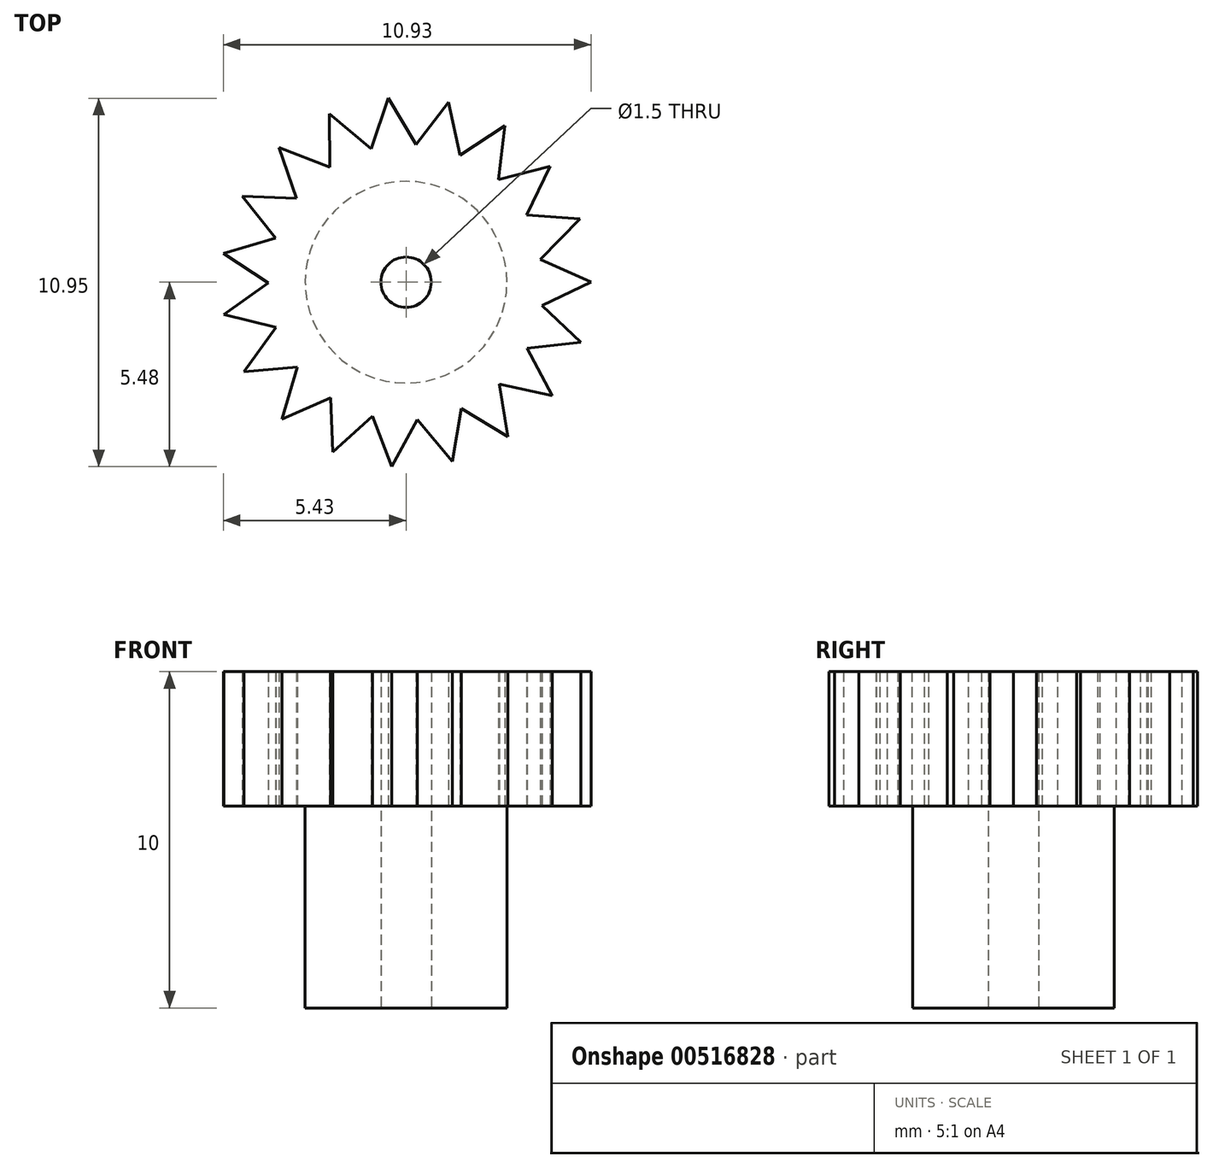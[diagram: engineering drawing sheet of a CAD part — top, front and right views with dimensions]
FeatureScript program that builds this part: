
annotation { "Feature Type Name" : "Feature", "Feature Type Description" : "" }
export const myFeature = defineFeature(function(context is Context, id is Id, definition is map)
    precondition{}
    {
        {
            var Q0;
            Q0=qCreatedBy(makeId("Top.planeOp"),FACE);
            var sketch = newSketch(context, id + "F0", { "sketchPlane" : qUnion([Q0])});
            skCircle(sketch, "E0", {"center": v(0, 0) * mm, "radius": 3 * mm});
            skSolve(sketch);
        }
        {
            var Q0;
            Q0 = qSketchRegion(id + "F0", true);
            extrude(context, id + "F1", {"entities" : qUnion([Q0]), "depth" : 6 * mm, "offsetDistance" : 25.4 * mm});
        }
        {
            var Q0;
            Q0=makeQuery(id+"F1.opExtrude","CAP_FACE",FACE,{"disambiguationData":[OSD([sQuery(id+"F0.wireOp",EDGE,"E0")])],"isStart":false});
            var sketch = newSketch(context, id + "F2", { "sketchPlane" : qUnion([Q0])});
            skLineSegment(sketch, "E1", {"start": v(5.5, 0) * mm, "end": v(3.99, 0.68) * mm});
            skLineSegment(sketch, "E2", {"start": v(5.5, 0) * mm, "end": v(4.04, -0.7) * mm});
            skPoint(sketch, "E3.start.orphan", {"position": v(4, 0) * mm});
            skLineSegment(sketch, "E4.1.0", {"start": v(5.2, -1.78) * mm, "end": v(4.04, -0.7) * mm});
            skLineSegment(sketch, "E4.1.1", {"start": v(5.2, -1.78) * mm, "end": v(3.6, -1.96) * mm});
            skLineSegment(sketch, "E4.2.0", {"start": v(4.35, -3.37) * mm, "end": v(3.6, -1.96) * mm});
            skLineSegment(sketch, "E4.2.1", {"start": v(4.35, -3.37) * mm, "end": v(2.77, -3.02) * mm});
            skLineSegment(sketch, "E4.3.0", {"start": v(3.02, -4.6) * mm, "end": v(2.77, -3.02) * mm});
            skLineSegment(sketch, "E4.3.1", {"start": v(3.02, -4.6) * mm, "end": v(1.64, -3.76) * mm});
            skLineSegment(sketch, "E4.4.0", {"start": v(1.37, -5.33) * mm, "end": v(1.64, -3.76) * mm});
            skLineSegment(sketch, "E4.4.1", {"start": v(1.37, -5.33) * mm, "end": v(0.34, -4.09) * mm});
            skLineSegment(sketch, "E4.5.0", {"start": v(-0.43, -5.48) * mm, "end": v(0.34, -4.09) * mm});
            skLineSegment(sketch, "E4.5.1", {"start": v(-0.43, -5.48) * mm, "end": v(-1, -3.98) * mm});
            skLineSegment(sketch, "E4.6.0", {"start": v(-2.18, -5.05) * mm, "end": v(-1, -3.98) * mm});
            skLineSegment(sketch, "E4.6.1", {"start": v(-2.18, -5.05) * mm, "end": v(-2.24, -3.44) * mm});
            skLineSegment(sketch, "E4.7.0", {"start": v(-3.7, -4.07) * mm, "end": v(-2.24, -3.44) * mm});
            skLineSegment(sketch, "E4.7.1", {"start": v(-3.7, -4.07) * mm, "end": v(-3.23, -2.53) * mm});
            skLineSegment(sketch, "E4.8.0", {"start": v(-4.82, -2.66) * mm, "end": v(-3.23, -2.53) * mm});
            skLineSegment(sketch, "E4.8.1", {"start": v(-4.82, -2.66) * mm, "end": v(-3.87, -1.35) * mm});
            skLineSegment(sketch, "E4.9.0", {"start": v(-5.42, -0.96) * mm, "end": v(-3.87, -1.35) * mm});
            skLineSegment(sketch, "E4.9.1", {"start": v(-5.42, -0.96) * mm, "end": v(-4.1, -0.02) * mm});
            skLineSegment(sketch, "E4.10.0", {"start": v(-5.43, 0.85) * mm, "end": v(-4.1, -0.02) * mm});
            skLineSegment(sketch, "E4.10.1", {"start": v(-5.43, 0.85) * mm, "end": v(-3.89, 1.3) * mm});
            skLineSegment(sketch, "E4.11.0", {"start": v(-4.87, 2.56) * mm, "end": v(-3.89, 1.3) * mm});
            skLineSegment(sketch, "E4.11.1", {"start": v(-4.87, 2.56) * mm, "end": v(-3.25, 2.5) * mm});
            skLineSegment(sketch, "E4.12.0", {"start": v(-3.77, 4) * mm, "end": v(-3.25, 2.5) * mm});
            skLineSegment(sketch, "E4.12.1", {"start": v(-3.77, 4) * mm, "end": v(-2.27, 3.42) * mm});
            skLineSegment(sketch, "E4.13.0", {"start": v(-2.28, 5) * mm, "end": v(-2.27, 3.42) * mm});
            skLineSegment(sketch, "E4.13.1", {"start": v(-2.28, 5) * mm, "end": v(-1.04, 3.97) * mm});
            skLineSegment(sketch, "E4.14.0", {"start": v(-0.53, 5.47) * mm, "end": v(-1.04, 3.97) * mm});
            skLineSegment(sketch, "E4.14.1", {"start": v(-0.53, 5.47) * mm, "end": v(0.3, 4.1) * mm});
            skLineSegment(sketch, "E4.15.0", {"start": v(1.27, 5.35) * mm, "end": v(0.3, 4.1) * mm});
            skLineSegment(sketch, "E4.15.1", {"start": v(1.27, 5.35) * mm, "end": v(1.6, 3.77) * mm});
            skLineSegment(sketch, "E4.16.0", {"start": v(2.93, 4.65) * mm, "end": v(1.6, 3.77) * mm});
            skLineSegment(sketch, "E4.16.1", {"start": v(2.93, 4.65) * mm, "end": v(2.74, 3.05) * mm});
            skLineSegment(sketch, "E4.17.0", {"start": v(4.28, 3.45) * mm, "end": v(2.74, 3.05) * mm});
            skLineSegment(sketch, "E4.17.1", {"start": v(4.28, 3.45) * mm, "end": v(3.58, 2) * mm});
            skLineSegment(sketch, "E4.18.0", {"start": v(5.17, 1.88) * mm, "end": v(3.58, 2) * mm});
            skLineSegment(sketch, "E4.18.1", {"start": v(5.17, 1.88) * mm, "end": v(3.99, 0.68) * mm});
            skPoint(sketch, "E4.center", {"position": v(0, 0) * mm});
            skPoint(sketch, "E5.orphan", {"position": v(-2.27, 3.3) * mm});
            skPoint(sketch, "E6.orphan", {"position": v(-3.21, 2.38) * mm});
            skPoint(sketch, "E7.orphan", {"position": v(-3.13, 2.5) * mm});
            skPoint(sketch, "E8.orphan", {"position": v(-3.81, 1.21) * mm});
            skPoint(sketch, "E9.orphan", {"position": v(-3.77, 1.35) * mm});
            skPoint(sketch, "E10.orphan", {"position": v(-4, -0.09) * mm});
            skPoint(sketch, "E11.orphan", {"position": v(-4, 0.05) * mm});
            skPoint(sketch, "E12.orphan", {"position": v(-3.76, -1.38) * mm});
            skPoint(sketch, "E13.orphan", {"position": v(-3.8, -1.24) * mm});
            skPoint(sketch, "E14.orphan", {"position": v(-2.24, -3.31) * mm});
            skPoint(sketch, "E15.orphan", {"position": v(-2.13, -3.39) * mm});
            skPoint(sketch, "E16.orphan", {"position": v(-0.91, -3.9) * mm});
            skPoint(sketch, "E17.orphan", {"position": v(-1.05, -3.86) * mm});
            skPoint(sketch, "E18.orphan", {"position": v(0.4, -3.98) * mm});
            skPoint(sketch, "E19.orphan", {"position": v(0.26, -4) * mm});
            skPoint(sketch, "E20.orphan", {"position": v(1.53, -3.7) * mm});
            skPoint(sketch, "E21.orphan", {"position": v(1.66, -3.64) * mm});
            skPoint(sketch, "E22.orphan", {"position": v(2.65, -3) * mm});
            skPoint(sketch, "E23.orphan", {"position": v(2.75, -2.9) * mm});
            skPoint(sketch, "E24.orphan", {"position": v(3.48, -1.98) * mm});
            skPoint(sketch, "E25.orphan", {"position": v(3.93, -0.75) * mm});
            skPoint(sketch, "E26.orphan", {"position": v(3.95, -0.6) * mm});
            skPoint(sketch, "E27.orphan", {"position": v(-2.15, 3.37) * mm});
            skPoint(sketch, "E28.orphan", {"position": v(-0.95, 3.89) * mm});
            skPoint(sketch, "E29.orphan", {"position": v(-1.08, 3.85) * mm});
            skPoint(sketch, "E30.orphan", {"position": v(0.36, 3.98) * mm});
            skPoint(sketch, "E31.orphan", {"position": v(0.22, 4) * mm});
            skPoint(sketch, "E32.orphan", {"position": v(1.5, 3.7) * mm});
            skPoint(sketch, "E33.orphan", {"position": v(1.63, 3.65) * mm});
            skPoint(sketch, "E34.orphan", {"position": v(2.62, 3.02) * mm});
            skPoint(sketch, "E35.orphan", {"position": v(2.73, 2.93) * mm});
            skPoint(sketch, "E36.orphan", {"position": v(3.95, 0.64) * mm});
            skSolve(sketch);
        }
        {
            var Q0;
            Q0=makeQuery(id+"F2.imprint","IMPRINT",FACE,{"disambiguationData":[TD([[makeQuery(id+"F2.imprint","IMPRINT",EDGE,{"derivedFrom":sQuery(id+"F2.wireOp",EDGE,"E1")}),1.0]])]});
            var Q1;
            Q1=makeQuery(id+"F2.imprint","IMPRINT",FACE,{"disambiguationData":[TD([[makeQuery(id+"F2.imprint","IMPRINT",EDGE,{"derivedFrom":makeQuery(id+"F1.opExtrude","CAP_EDGE",EDGE,{"disambiguationData":[OSD([sQuery(id+"F0.wireOp",EDGE,"E0")])],"isStart":false})}),1.0]])]});
            extrude(context, id + "F3", {"entities" : qUnion([Q0, Q1]), "operationType" : NewBodyOperationType.ADD, "depth" : 4 * mm, "offsetDistance" : 25.4 * mm});
        }
        {
            var Q0;
            Q0=makeQuery(id+"F1.opExtrude","CAP_FACE",FACE,{"disambiguationData":[OSD([sQuery(id+"F0.wireOp",EDGE,"E0")])],"isStart":true});
            var sketch = newSketch(context, id + "F4", { "sketchPlane" : qUnion([Q0])});
            skCircle(sketch, "E37", {"center": v(0, 0) * mm, "radius": 0.75 * mm});
            skSolve(sketch);
        }
        {
            var Q0;
            Q0=makeQuery(id+"F4.imprint","IMPRINT",FACE,{"disambiguationData":[TD([[makeQuery(id+"F4.imprint","IMPRINT",EDGE,{"derivedFrom":sQuery(id+"F4.wireOp",EDGE,"E37")}),1.0]])]});
            extrude(context, id + "F5", {"entities" : qUnion([Q0]), "operationType" : NewBodyOperationType.REMOVE, "oppositeDirection" : true, "depth" : 25.4 * mm, "offsetDistance" : 25.4 * mm});
        }
    });
